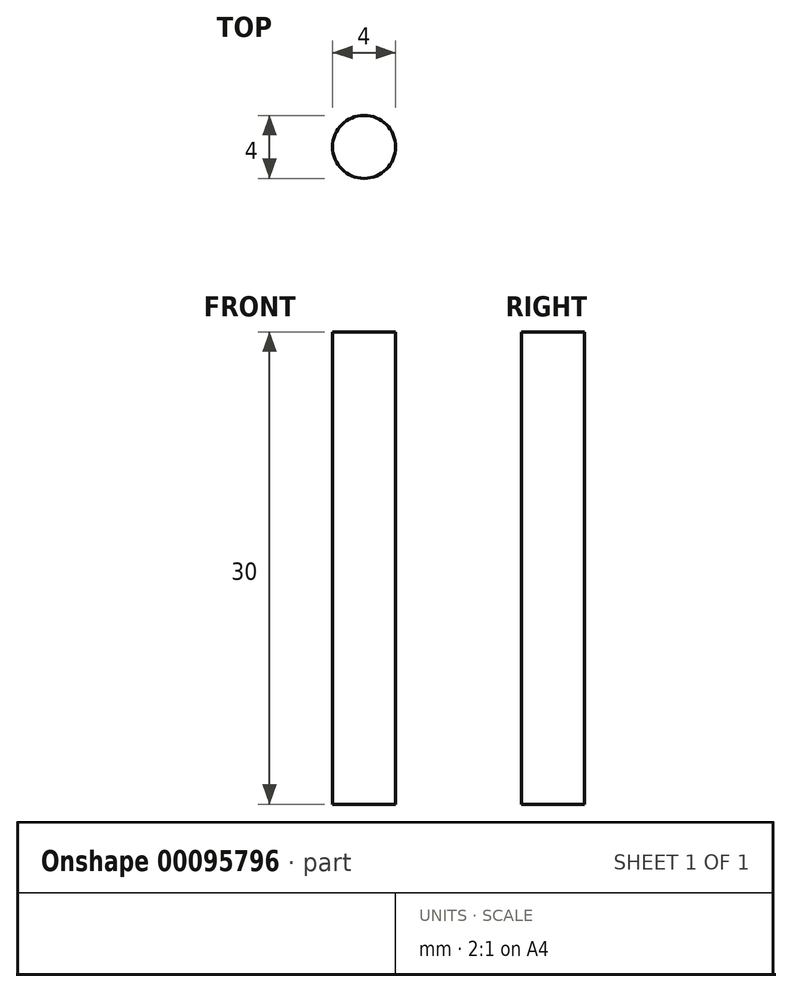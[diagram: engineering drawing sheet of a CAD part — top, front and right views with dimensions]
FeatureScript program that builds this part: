
annotation { "Feature Type Name" : "Feature", "Feature Type Description" : "" }
export const myFeature = defineFeature(function(context is Context, id is Id, definition is map)
    precondition{}
    {
        {
            var Q0;
            Q0=qCreatedBy(makeId("Top.planeOp"),FACE);
            var sketch = newSketch(context, id + "F0", { "sketchPlane" : qUnion([Q0])});
            skCircle(sketch, "E0", {"center": v(0, 0) * mm, "radius": 2 * mm});
            skSolve(sketch);
        }
        {
            var Q0;
            Q0 = qSketchRegion(id + "F0", true);
            extrude(context, id + "F1", {"entities" : qUnion([Q0]), "endBound" : BoundingType.SYMMETRIC, "depth" : 30 * mm});
        }
    });
